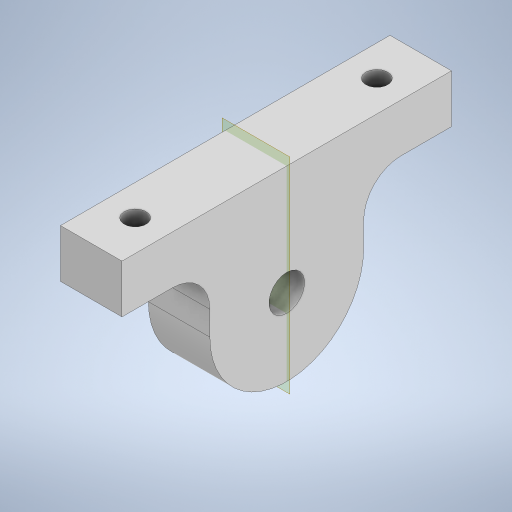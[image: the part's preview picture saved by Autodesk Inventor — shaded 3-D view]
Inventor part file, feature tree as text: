
AUTODESK INVENTOR PART (.ipt)
format: ipt  version: 2024 (Build 280153020, 153B)  size: 269,312 bytes
history: native  units: mm
features: sketch x4, extrude x3, plane x1, fillet x1, hole x1, mirror x1
ambient origin geometry x8: Origin, YZ Plane, XZ Plane, XY Plane, X Axis, Y Axis, Z Axis, Center Point
bodies: Solid1 (feature_tree)
feature tree (11):
  extrude  "Extrusion1"  Depth=35.0mm
  plane  "Work Plane1"
  extrude  "Extrusion2"  Depth=25.0mm
  fillet  "Fillet1"  Radius=14.0mm
  hole  "Hole1"  [1 undecoded]
  extrude  "Extrusion3"  Depth=10.0mm
  mirror  "Mirror1"
  sketch  "Sketch1"  dims[d0=8.1mm d1=35.0mm]
  sketch  "Sketch2"  dims[d2=25.0mm d3=25.0mm d4=14.0mm d5=0.0mm]
  sketch  "Sketch3"  dims[d6=20.0mm d7=11.0mm]
  sketch  "Sketch4"  dims[d8=14.0mm d9=0.0mm d10=8.5mm d11=10.0mm d12=5.0mm d13=6.0mm d14=9.5mm d15=2.0mm d16=90.0deg d17=8.0mm d18=20.594885mm d19=14.0mm d20=0.0mm]
note: 1 required parameter value undecoded (feature->parameter linkage not recoverable at this tier; creation-order binding heuristic only, values carry confidence <= 0.55)
